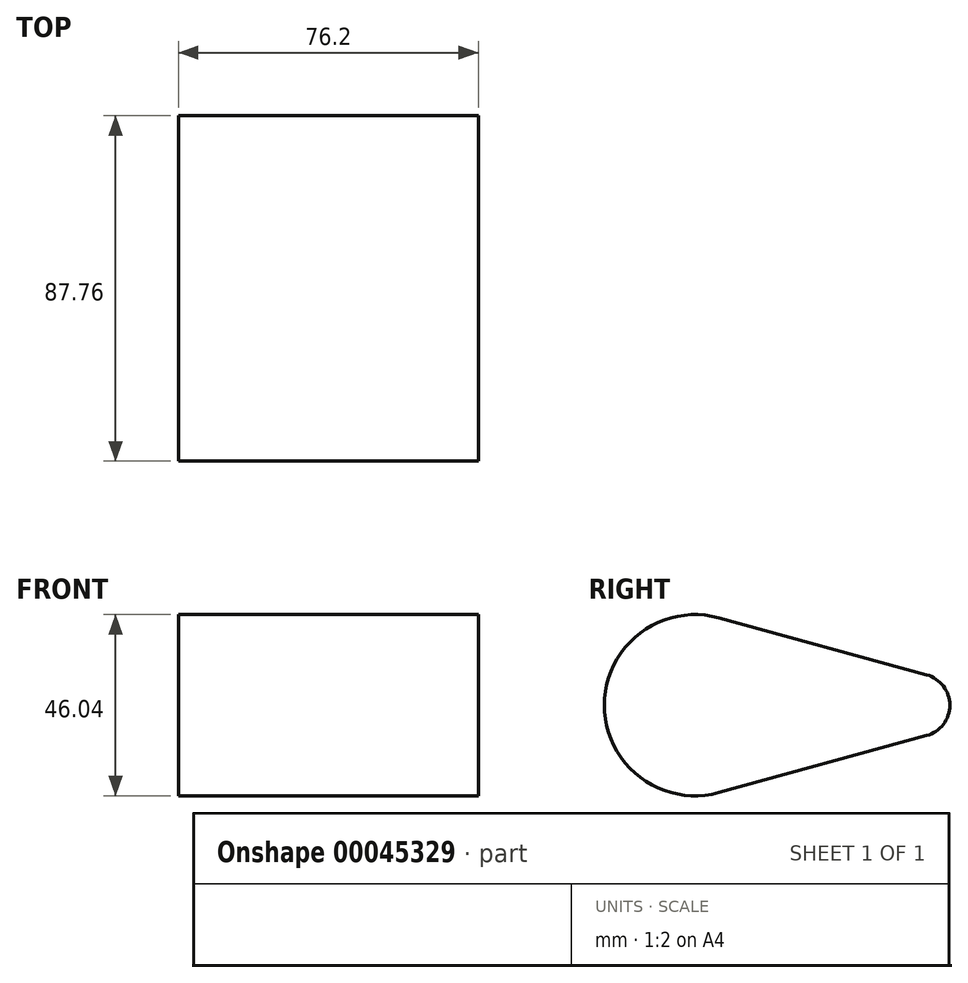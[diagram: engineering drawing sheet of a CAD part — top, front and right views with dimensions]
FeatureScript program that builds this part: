
annotation { "Feature Type Name" : "Feature", "Feature Type Description" : "" }
export const myFeature = defineFeature(function(context is Context, id is Id, definition is map)
    precondition{}
    {
        {
            var Q0;
            Q0=qCreatedBy(makeId("Right.planeOp"),FACE);
            var sketch = newSketch(context, id + "F0", { "sketchPlane" : qUnion([Q0])});
            skCircle(sketch, "E0", {"center": v(0, 0) * mm, "radius": 23.02 * mm});
            skCircle(sketch, "E1", {"center": v(56.75, 0) * mm, "radius": 8 * mm});
            skLineSegment(sketch, "E2", {"start": v(6.1, 22.2) * mm, "end": v(58.87, 7.7) * mm});
            skLineSegment(sketch, "E3", {"start": v(6.1, -22.2) * mm, "end": v(58.87, -7.7) * mm});
            skSolve(sketch);
        }
        {
            var Q0;
            {var subQ0=sQuery(id+"F0.wireOp",EDGE,"E1");var subQ2=makeQuery(id+"F0.imprint","INTERSECT",VERTEX,{"derivedFrom":[subQ0,sQuery(id+"F0.wireOp",EDGE,"E2")]});Q0=makeQuery(id+"F0.imprint","IMPRINT",FACE,{"disambiguationData":[TD([[makeQuery(id+"F0.imprint","IMPRINT",EDGE,{"disambiguationData":[TD([[subQ2,-1.0]])],"derivedFrom":subQ0}),1.0]])]});}
            var Q1;
            {var subQ0=sQuery(id+"F0.wireOp",EDGE,"E0");var subQ2=makeQuery(id+"F0.imprint","INTERSECT",VERTEX,{"derivedFrom":[subQ0,sQuery(id+"F0.wireOp",EDGE,"E2")]});Q1=makeQuery(id+"F0.imprint","IMPRINT",FACE,{"disambiguationData":[TD([[makeQuery(id+"F0.imprint","IMPRINT",EDGE,{"disambiguationData":[TD([[subQ2,-1.0]])],"derivedFrom":subQ0}),1.0]])]});}
            var Q2;
            {var subQ1=sQuery(id+"F0.wireOp",EDGE,"E2");Q2=makeQuery(id+"F0.imprint","IMPRINT",FACE,{"disambiguationData":[TD([[makeQuery(id+"F0.imprint","IMPRINT",EDGE,{"derivedFrom":subQ1}),-1.0]])]});}
            extrude(context, id + "F1", {"entities" : qUnion([Q0, Q1, Q2]), "depth" : 76.2 * mm});
        }
    });
